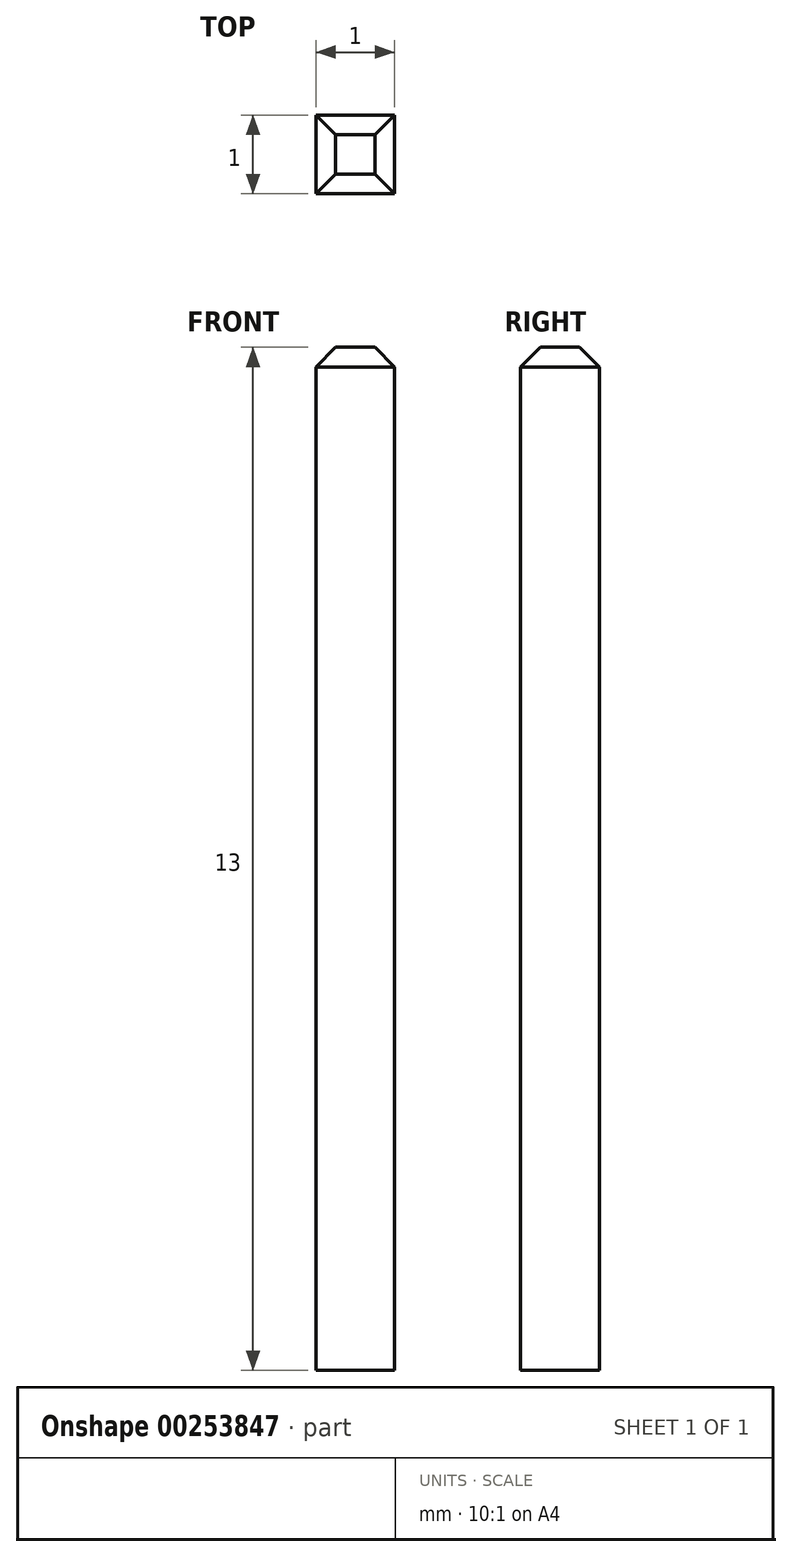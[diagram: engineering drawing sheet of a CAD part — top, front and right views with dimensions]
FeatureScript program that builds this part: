
annotation { "Feature Type Name" : "Feature", "Feature Type Description" : "" }
export const myFeature = defineFeature(function(context is Context, id is Id, definition is map)
    precondition{}
    {
        {
            var Q0;
            Q0=qCreatedBy(makeId("Top.planeOp"),FACE);
            var sketch = newSketch(context, id + "F0", { "sketchPlane" : qUnion([Q0])});
            skLineSegment(sketch, "E0.bottom", {"start": v(0, 0) * mm, "end": v(1, 0) * mm});
            skLineSegment(sketch, "E0.top", {"start": v(0, 1) * mm, "end": v(1, 1) * mm});
            skLineSegment(sketch, "E0.left", {"start": v(0, 0) * mm, "end": v(0, 1) * mm});
            skLineSegment(sketch, "E0.right", {"start": v(1, 0) * mm, "end": v(1, 1) * mm});
            skSolve(sketch);
        }
        {
            var Q0;
            Q0 = qSketchRegion(id + "F0", true);
            extrude(context, id + "F1", {"entities" : qUnion([Q0]), "depth" : 13 * mm});
        }
        {
            var Q0;
            Q0=makeQuery(id+"F1.opExtrude","CAP_EDGE",EDGE,{"disambiguationData":[OSD([sQuery(id+"F0.wireOp",EDGE,"E0.bottom")])],"isStart":false});
            var Q1;
            Q1=makeQuery(id+"F1.opExtrude","CAP_EDGE",EDGE,{"disambiguationData":[OSD([sQuery(id+"F0.wireOp",EDGE,"E0.right")])],"isStart":false});
            var Q2;
            Q2=makeQuery(id+"F1.opExtrude","CAP_EDGE",EDGE,{"disambiguationData":[OSD([sQuery(id+"F0.wireOp",EDGE,"E0.top")])],"isStart":false});
            var Q3;
            Q3=makeQuery(id+"F1.opExtrude","CAP_EDGE",EDGE,{"disambiguationData":[OSD([sQuery(id+"F0.wireOp",EDGE,"E0.left")])],"isStart":false});
            chamfer(context, id + "F2", {"entities" : qUnion([Q0, Q1, Q2, Q3]), "width" : 0.25 * mm, "tangentPropagation" : true});
        }
    });
